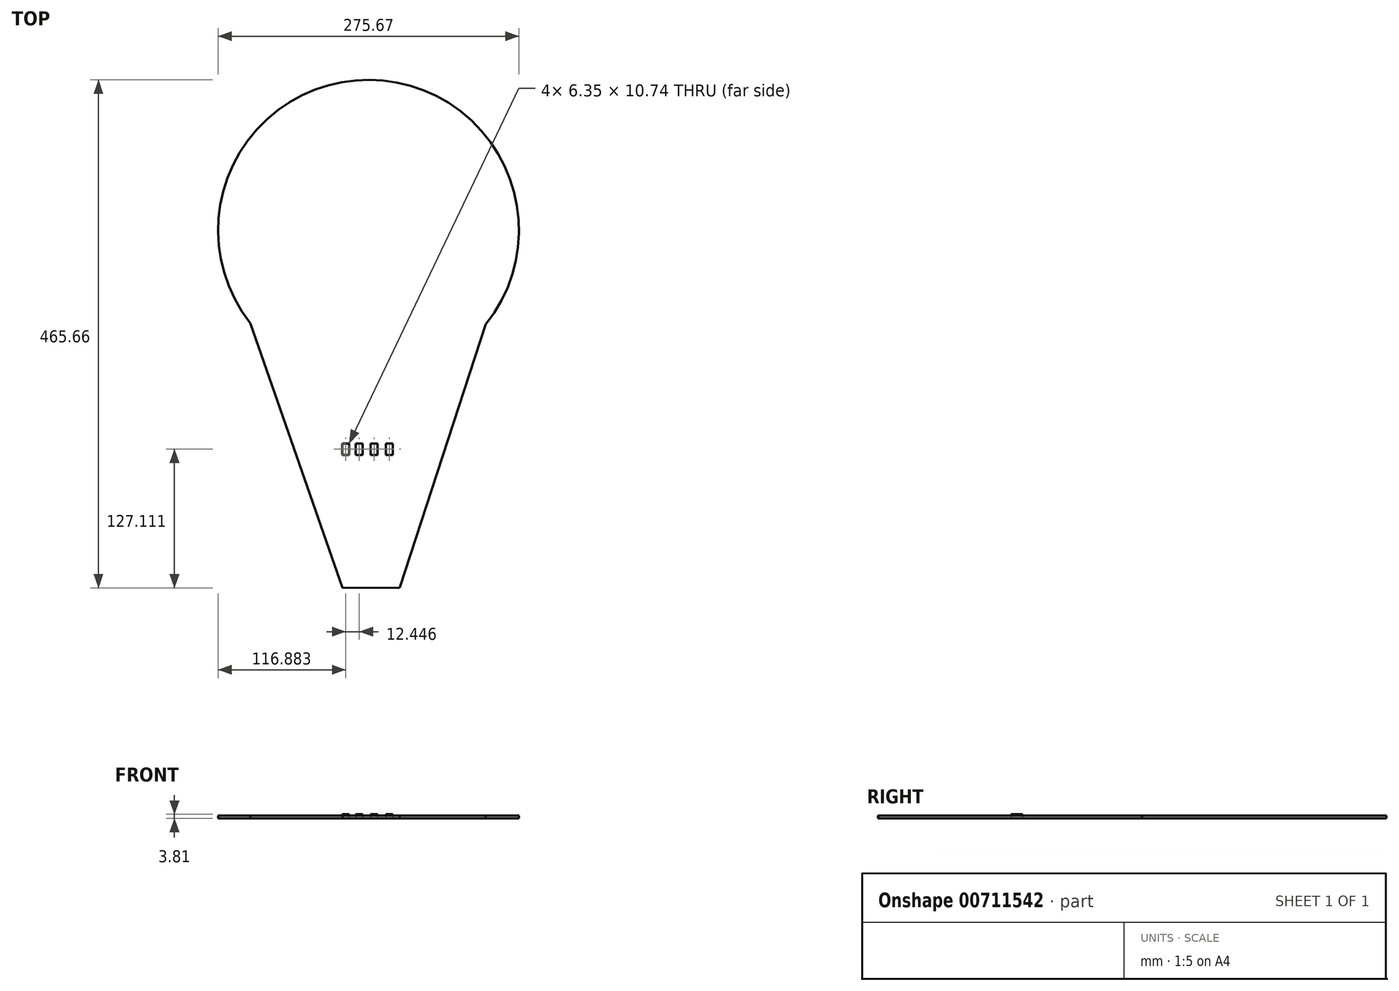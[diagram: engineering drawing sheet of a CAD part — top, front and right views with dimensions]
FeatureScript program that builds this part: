
annotation { "Feature Type Name" : "Feature", "Feature Type Description" : "" }
export const myFeature = defineFeature(function(context is Context, id is Id, definition is map)
    precondition{}
    {
        {
            var Q0;
            Q0=qCreatedBy(makeId("Top.planeOp"),FACE);
            var sketch = newSketch(context, id + "F0", { "sketchPlane" : qUnion([Q0])});
            skArc(sketch, "E0", {"start": v(148.74, 177.02) * mm, "mid": v(42, 401.18) * mm, "end": v(-67.05, 178.14) * mm});
            skLineSegment(sketch, "E1", {"start": v(43.2, -64.32) * mm, "end": v(69.96, -64.16) * mm});
            skLineSegment(sketch, "E2", {"start": v(43.2, -64.32) * mm, "end": v(17.46, -64.47) * mm});
            skLineSegment(sketch, "E3", {"start": v(-67.05, 178.14) * mm, "end": v(17.46, -64.47) * mm});
            skLineSegment(sketch, "E4", {"start": v(148.74, 177.02) * mm, "end": v(69.96, -64.16) * mm});
            skLineSegment(sketch, "E5", {"start": v(17.46, -64.47) * mm, "end": v(17.16, -13) * mm});
            skLineSegment(sketch, "E6", {"start": v(17.16, -13) * mm, "end": v(23.74, -12.97) * mm});
            skLineSegment(sketch, "E7", {"start": v(69.96, -64.16) * mm, "end": v(69.65, -11.95) * mm});
            skLineSegment(sketch, "E8", {"start": v(69.65, -11.95) * mm, "end": v(63.08, -11.95) * mm});
            skLineSegment(sketch, "E9.bottom", {"start": v(17.16, 68) * mm, "end": v(23.5, 68) * mm});
            skLineSegment(sketch, "E9.top", {"start": v(17.16, 57.27) * mm, "end": v(23.5, 57.27) * mm});
            skLineSegment(sketch, "E9.left", {"start": v(17.16, 68) * mm, "end": v(17.16, 57.27) * mm});
            skLineSegment(sketch, "E9.right", {"start": v(23.5, 68) * mm, "end": v(23.5, 57.27) * mm});
            skLineSegment(sketch, "E10.bottom", {"start": v(29.6, 68) * mm, "end": v(35.95, 68) * mm});
            skLineSegment(sketch, "E10.top", {"start": v(29.6, 57.27) * mm, "end": v(35.95, 57.27) * mm});
            skLineSegment(sketch, "E10.left", {"start": v(29.6, 68) * mm, "end": v(29.6, 57.27) * mm});
            skLineSegment(sketch, "E10.right", {"start": v(35.95, 68) * mm, "end": v(35.95, 57.27) * mm});
            skLineSegment(sketch, "E11.bottom", {"start": v(43.07, 68) * mm, "end": v(49.42, 68) * mm});
            skLineSegment(sketch, "E11.top", {"start": v(43.07, 57.27) * mm, "end": v(49.42, 57.27) * mm});
            skLineSegment(sketch, "E11.left", {"start": v(43.07, 68) * mm, "end": v(43.07, 57.27) * mm});
            skLineSegment(sketch, "E11.right", {"start": v(49.42, 68) * mm, "end": v(49.42, 57.27) * mm});
            skLineSegment(sketch, "E12.bottom", {"start": v(57.04, 68) * mm, "end": v(63.39, 68) * mm});
            skLineSegment(sketch, "E12.top", {"start": v(57.04, 57.27) * mm, "end": v(63.39, 57.27) * mm});
            skLineSegment(sketch, "E12.left", {"start": v(57.04, 68) * mm, "end": v(57.04, 57.27) * mm});
            skLineSegment(sketch, "E12.right", {"start": v(63.39, 68) * mm, "end": v(63.39, 57.27) * mm});
            skArc(sketch, "E13", {"start": v(145.16, 191.3) * mm, "mid": v(165.94, 243.24) * mm, "end": v(162, 299.05) * mm});
            skArc(sketch, "E14", {"start": v(-80.46, 286.4) * mm, "mid": v(-80.65, 239.72) * mm, "end": v(-63.72, 196.23) * mm});
            skArc(sketch, "E15", {"start": v(79.49, 384) * mm, "mid": v(38.63, 389.57) * mm, "end": v(-1.86, 381.81) * mm});
            skLineSegment(sketch, "E16", {"start": v(43.2, 353.66) * mm, "end": v(68.4, 353.66) * mm});
            skLineSegment(sketch, "E17", {"start": v(43.2, 353.66) * mm, "end": v(18.3, 353.66) * mm});
            skLineSegment(sketch, "E18", {"start": v(43.42, 350.32) * mm, "end": v(68.62, 350.32) * mm});
            skLineSegment(sketch, "E19", {"start": v(43.42, 350.32) * mm, "end": v(18.54, 350.32) * mm});
            skLineSegment(sketch, "E20", {"start": v(42.74, 346.25) * mm, "end": v(67.95, 346.25) * mm});
            skLineSegment(sketch, "E21", {"start": v(42.74, 346.25) * mm, "end": v(17.86, 346.25) * mm});
            skLineSegment(sketch, "E22", {"start": v(42.45, 338.91) * mm, "end": v(67.66, 338.91) * mm});
            skLineSegment(sketch, "E23", {"start": v(42.45, 338.91) * mm, "end": v(17.57, 338.91) * mm});
            skLineSegment(sketch, "E24", {"start": v(17.46, -64.47) * mm, "end": v(23.82, -64.43) * mm});
            skLineSegment(sketch, "E25", {"start": v(69.96, -64.16) * mm, "end": v(64.25, -64.2) * mm});
            skSolve(sketch);
        }
        {
            var Q0;
            Q0=sQuery(id+"F0.wireOp",EDGE,"E0");
            extrude(context, id + "F1", {"bodyType" : ToolBodyType.SURFACE, "surfaceEntities" : qUnion([Q0]), "depth" : 25.4 * mm, "offsetDistance" : 25.4 * mm});
        }
        {
            var Q0;
            Q0=sQuery(id+"F0.wireOp",EDGE,"E4");
            extrude(context, id + "F2", {"bodyType" : ToolBodyType.SURFACE, "surfaceEntities" : qUnion([Q0]), "depth" : 25.4 * mm, "offsetDistance" : 25.4 * mm});
        }
        {
            var Q0;
            Q0=sQuery(id+"F0.wireOp",EDGE,"E3");
            extrude(context, id + "F3", {"bodyType" : ToolBodyType.SURFACE, "surfaceEntities" : qUnion([Q0]), "depth" : 25.4 * mm, "offsetDistance" : 25.4 * mm});
        }
        {
            var Q0;
            Q0=sQuery(id+"F0.wireOp",EDGE,"E5");
            var Q1;
            Q1=sQuery(id+"F0.wireOp",EDGE,"E6");
            var Q2;
            Q2=sQuery(id+"F0.wireOp",EDGE,"E8");
            var Q3;
            Q3=sQuery(id+"F0.wireOp",EDGE,"E7");
            extrude(context, id + "F4", {"bodyType" : ToolBodyType.SURFACE, "surfaceEntities" : qUnion([Q0, Q1, Q2, Q3]), "depth" : 25.4 * mm, "offsetDistance" : 25.4 * mm});
        }
        {
            var Q0;
            Q0=makeQuery(id+"F0.imprint","IMPRINT",FACE,{"disambiguationData":[TD([[makeQuery(id+"F0.imprint","IMPRINT",EDGE,{"derivedFrom":sQuery(id+"F0.wireOp",EDGE,"E9.bottom")}),-1.0]])]});
            var Q1;
            Q1=makeQuery(id+"F0.imprint","IMPRINT",FACE,{"disambiguationData":[TD([[makeQuery(id+"F0.imprint","IMPRINT",EDGE,{"derivedFrom":sQuery(id+"F0.wireOp",EDGE,"E10.bottom")}),-1.0]])]});
            var Q2;
            Q2=makeQuery(id+"F0.imprint","IMPRINT",FACE,{"disambiguationData":[TD([[makeQuery(id+"F0.imprint","IMPRINT",EDGE,{"derivedFrom":sQuery(id+"F0.wireOp",EDGE,"E11.bottom")}),-1.0]])]});
            var Q3;
            Q3=makeQuery(id+"F0.imprint","IMPRINT",FACE,{"disambiguationData":[TD([[makeQuery(id+"F0.imprint","IMPRINT",EDGE,{"derivedFrom":sQuery(id+"F0.wireOp",EDGE,"E12.bottom")}),-1.0]])]});
            extrude(context, id + "F5", {"entities" : qUnion([Q0, Q1, Q2, Q3]), "depth" : 3.8 * mm, "offsetDistance" : 25.4 * mm});
        }
        {
            var Q0;
            Q0=makeQuery(id+"F0.imprint","IMPRINT",FACE,{"disambiguationData":[TD([[makeQuery(id+"F0.imprint","IMPRINT",EDGE,{"derivedFrom":sQuery(id+"F0.wireOp",EDGE,"E0")}),1.0]])]});
            extrude(context, id + "F6", {"entities" : qUnion([Q0]), "depth" : 2.54 * mm, "offsetDistance" : 25.4 * mm});
        }
        {
            var Q0;
            Q0=sQuery(id+"F0.wireOp",EDGE,"E14");
            extrude(context, id + "F7", {"bodyType" : ToolBodyType.SURFACE, "surfaceEntities" : qUnion([Q0]), "depth" : 22.86 * mm, "offsetDistance" : 25.4 * mm});
        }
        {
            var Q0;
            Q0=sQuery(id+"F0.wireOp",EDGE,"E15");
            var Q1;
            Q1=sQuery(id+"F0.wireOp",EDGE,"E13");
            extrude(context, id + "F8", {"bodyType" : ToolBodyType.SURFACE, "surfaceEntities" : qUnion([Q0, Q1]), "depth" : 22.86 * mm, "offsetDistance" : 25.4 * mm});
        }
        {
            var Q0;
            Q0=sQuery(id+"F0.wireOp",EDGE,"E13");
            extrude(context, id + "F9", {"bodyType" : ToolBodyType.SURFACE, "surfaceEntities" : qUnion([Q0]), "depth" : 19.05 * mm, "offsetDistance" : 25.4 * mm});
        }
        {
            var Q0;
            Q0=sQuery(id+"F0.wireOp",EDGE,"E16");
            var Q1;
            Q1=sQuery(id+"F0.wireOp",EDGE,"E17");
            extrude(context, id + "F10", {"bodyType" : ToolBodyType.SURFACE, "surfaceEntities" : qUnion([Q0, Q1]), "depth" : 6.35 * mm, "offsetDistance" : 25.4 * mm});
        }
        {
            var Q0;
            Q0=sQuery(id+"F0.wireOp",EDGE,"E18");
            var Q1;
            Q1=sQuery(id+"F0.wireOp",EDGE,"E19");
            var Q2;
            Q2=sQuery(id+"F0.wireOp",EDGE,"E21");
            var Q3;
            Q3=sQuery(id+"F0.wireOp",EDGE,"E20");
            var Q4;
            Q4=sQuery(id+"F0.wireOp",EDGE,"E22");
            var Q5;
            Q5=sQuery(id+"F0.wireOp",EDGE,"E23");
            extrude(context, id + "F11", {"bodyType" : ToolBodyType.SURFACE, "surfaceEntities" : qUnion([Q0, Q1, Q2, Q3, Q4, Q5]), "depth" : 6.35 * mm, "offsetDistance" : 25.4 * mm});
        }
        {
            var Q0;
            Q0=sQuery(id+"F0.wireOp",EDGE,"E25");
            var Q1;
            Q1=sQuery(id+"F0.wireOp",EDGE,"E24");
            extrude(context, id + "F12", {"bodyType" : ToolBodyType.SURFACE, "surfaceEntities" : qUnion([Q0, Q1]), "depth" : 25.4 * mm, "offsetDistance" : 25.4 * mm});
        }
    });
